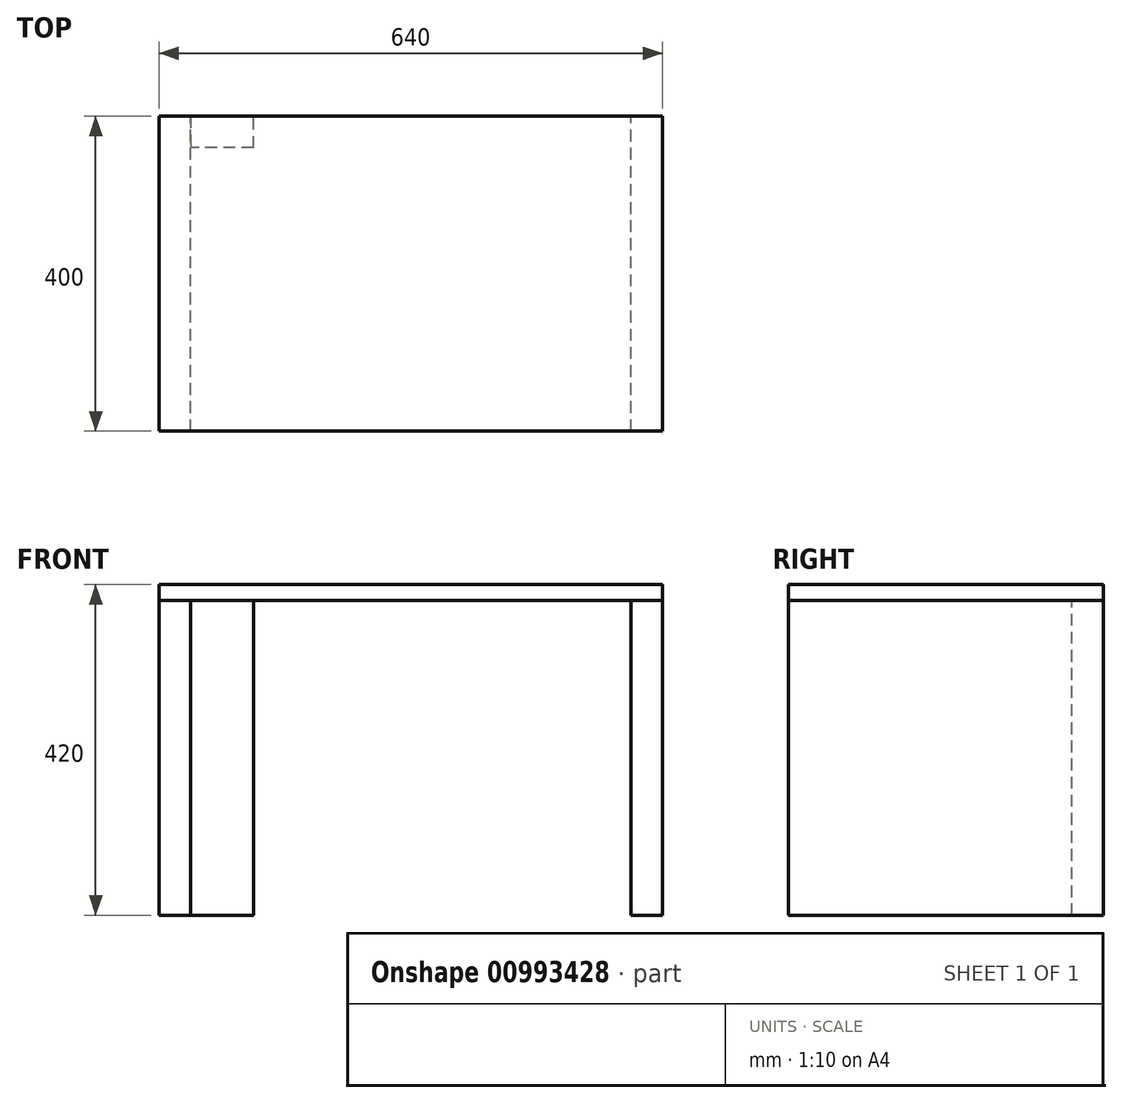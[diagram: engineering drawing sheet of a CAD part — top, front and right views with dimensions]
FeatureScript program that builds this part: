
annotation { "Feature Type Name" : "Feature", "Feature Type Description" : "" }
export const myFeature = defineFeature(function(context is Context, id is Id, definition is map)
    precondition{}
    {
        {
            var Q0;
            Q0=qCreatedBy(makeId("Top.planeOp"),FACE);
            var sketch = newSketch(context, id + "F0", { "sketchPlane" : qUnion([Q0])});
            skLineSegment(sketch, "E0.bottom", {"start": v(-135.68, -338.56) * mm, "end": v(504.32, -338.56) * mm});
            skLineSegment(sketch, "E0.top", {"start": v(-135.68, 61.44) * mm, "end": v(504.32, 61.44) * mm});
            skLineSegment(sketch, "E0.left", {"start": v(-135.68, -338.56) * mm, "end": v(-135.68, 61.44) * mm});
            skLineSegment(sketch, "E0.right", {"start": v(504.32, -338.56) * mm, "end": v(504.32, 61.44) * mm});
            skLineSegment(sketch, "E1.bottom", {"start": v(-135.68, -338.56) * mm, "end": v(-95.68, -338.56) * mm});
            skLineSegment(sketch, "E1.top", {"start": v(-135.68, 61.44) * mm, "end": v(-95.68, 61.44) * mm});
            skLineSegment(sketch, "E1.right", {"start": v(-95.68, -338.56) * mm, "end": v(-95.68, 61.44) * mm});
            skLineSegment(sketch, "E2.bottom", {"start": v(504.32, -338.56) * mm, "end": v(464.32, -338.56) * mm});
            skLineSegment(sketch, "E2.top", {"start": v(504.32, 61.44) * mm, "end": v(464.32, 61.44) * mm});
            skLineSegment(sketch, "E2.right", {"start": v(464.32, -338.56) * mm, "end": v(464.32, 61.44) * mm});
            skSolve(sketch);
        }
        {
            var Q0;
            {var subQ0=sQuery(id+"F0.wireOp",EDGE,"E1.right");Q0=makeQuery(id+"F0.imprint","IMPRINT",FACE,{"disambiguationData":[TD([[makeQuery(id+"F0.imprint","IMPRINT",EDGE,{"derivedFrom":subQ0}),-1.0]])]});}
            var Q1;
            {var subQ2=sQuery(id+"F0.wireOp",EDGE,"E0.left");Q1=makeQuery(id+"F0.imprint","IMPRINT",FACE,{"disambiguationData":[TD([[makeQuery(id+"F0.imprint","IMPRINT",EDGE,{"derivedFrom":subQ2}),-1.0]])]});}
            var Q2;
            {var subQ0=sQuery(id+"F0.wireOp",EDGE,"E0.right");Q2=makeQuery(id+"F0.imprint","IMPRINT",FACE,{"disambiguationData":[TD([[makeQuery(id+"F0.imprint","IMPRINT",EDGE,{"derivedFrom":subQ0}),1.0]])]});}
            extrude(context, id + "F1", {"entities" : qUnion([Q0, Q1, Q2]), "depth" : 20 * mm, "offsetDistance" : 25 * mm});
        }
        {
            var Q0;
            {var subQ2=sQuery(id+"F0.wireOp",EDGE,"E0.left");Q0=makeQuery(id+"F0.imprint","IMPRINT",FACE,{"disambiguationData":[TD([[makeQuery(id+"F0.imprint","IMPRINT",EDGE,{"derivedFrom":subQ2}),-1.0]])]});}
            var Q1;
            {var subQ0=sQuery(id+"F0.wireOp",EDGE,"E0.right");Q1=makeQuery(id+"F0.imprint","IMPRINT",FACE,{"disambiguationData":[TD([[makeQuery(id+"F0.imprint","IMPRINT",EDGE,{"derivedFrom":subQ0}),1.0]])]});}
            extrude(context, id + "F2", {"entities" : qUnion([Q0, Q1]), "oppositeDirection" : true, "depth" : 400 * mm, "offsetDistance" : 25 * mm});
        }
        {
            var Q0;
            {var subQ0=sQuery(id+"F0.wireOp",EDGE,"E1.right");Q0=makeQuery(id+"F0.imprint","IMPRINT",FACE,{"disambiguationData":[TD([[makeQuery(id+"F0.imprint","IMPRINT",EDGE,{"derivedFrom":subQ0}),-1.0]])]});}
            var sketch = newSketch(context, id + "F3", { "sketchPlane" : qUnion([Q0])});
            skPoint(sketch, "E3.0", {"position": v(-95.68, 61.44) * mm});
            skLineSegment(sketch, "E4.bottom", {"start": v(-95.68, 61.44) * mm, "end": v(-15.68, 61.44) * mm});
            skLineSegment(sketch, "E4.top", {"start": v(-95.68, 21.44) * mm, "end": v(-15.68, 21.44) * mm});
            skLineSegment(sketch, "E4.left", {"start": v(-95.68, 61.44) * mm, "end": v(-95.68, 21.44) * mm});
            skLineSegment(sketch, "E4.right", {"start": v(-15.68, 61.44) * mm, "end": v(-15.68, 21.44) * mm});
            skSolve(sketch);
        }
        {
            var Q0;
            Q0=makeQuery(id+"F3.imprint","IMPRINT",FACE,{"disambiguationData":[TD([[makeQuery(id+"F3.imprint","IMPRINT",EDGE,{"derivedFrom":sQuery(id+"F3.wireOp",EDGE,"E4.bottom")}),-1.0]])]});
            var Q1;
            Q1=makeQuery(id+"F2.opExtrude","CAP_FACE",FACE,{"disambiguationData":[OSD([sQuery(id+"F0.wireOp",EDGE,"E0.bottom"),sQuery(id+"F0.wireOp",EDGE,"E0.top"),sQuery(id+"F0.wireOp",EDGE,"E0.left"),sQuery(id+"F0.wireOp",EDGE,"E1.right")])],"isStart":false});
            extrude(context, id + "F4", {"entities" : qUnion([Q0]), "endBound" : BoundingType.UP_TO_SURFACE, "oppositeDirection" : true, "depth" : 25 * mm, "endBoundEntityFace" : qUnion([Q1]), "offsetDistance" : 25 * mm});
        }
    });
